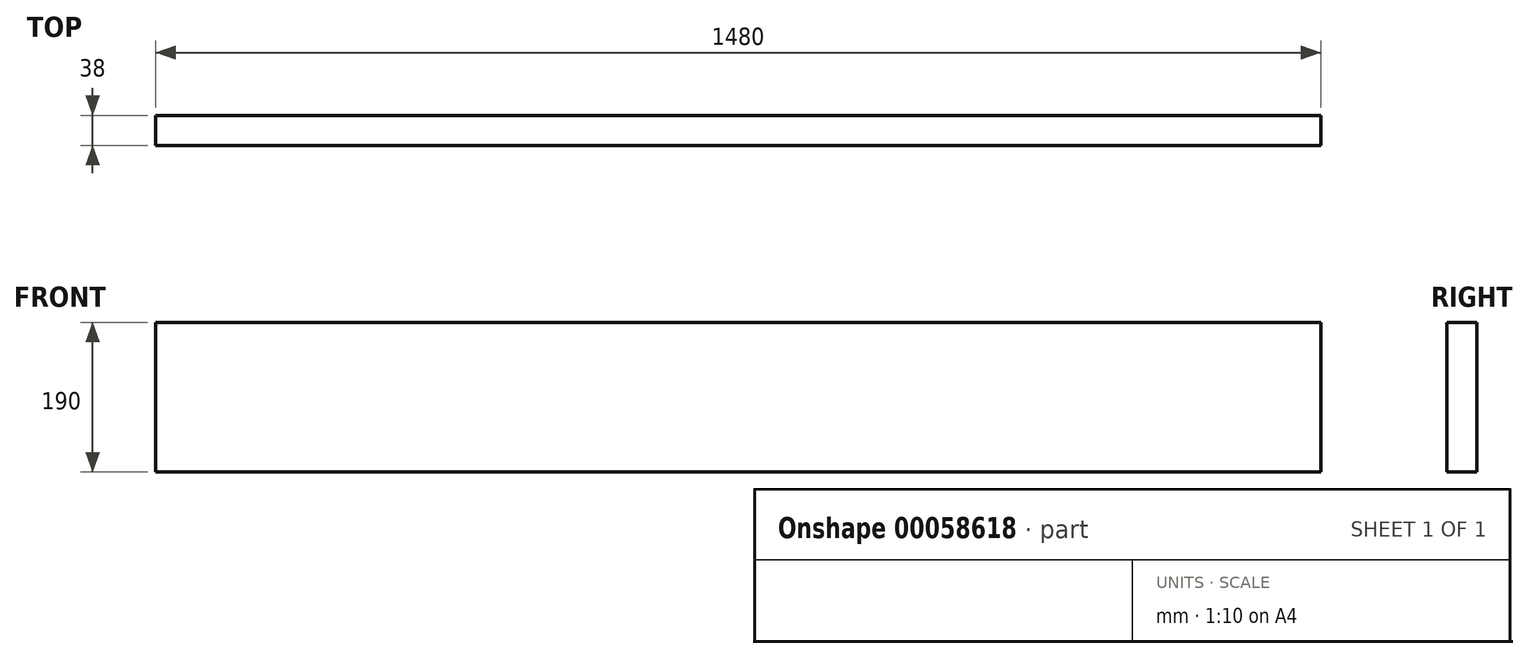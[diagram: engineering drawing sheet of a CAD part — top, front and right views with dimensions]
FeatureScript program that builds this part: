
annotation { "Feature Type Name" : "Feature", "Feature Type Description" : "" }
export const myFeature = defineFeature(function(context is Context, id is Id, definition is map)
    precondition{}
    {
        {
            var Q0;
            Q0=qCreatedBy(makeId("Front.planeOp"),FACE);
            var sketch = newSketch(context, id + "F0", { "sketchPlane" : qUnion([Q0])});
            skLineSegment(sketch, "E0.bottom", {"start": v(1480, 190) * mm, "end": v(0, 190) * mm});
            skLineSegment(sketch, "E0.top", {"start": v(1480, 0) * mm, "end": v(0, 0) * mm});
            skLineSegment(sketch, "E0.left", {"start": v(1480, 190) * mm, "end": v(1480, 0) * mm});
            skLineSegment(sketch, "E0.right", {"start": v(0, 190) * mm, "end": v(0, 0) * mm});
            skSolve(sketch);
        }
        {
            var Q0;
            Q0=makeQuery(id+"F0.imprint","IMPRINT",FACE,{"disambiguationData":[TD([[makeQuery(id+"F0.imprint","IMPRINT",EDGE,{"derivedFrom":sQuery(id+"F0.wireOp",EDGE,"E0.bottom")}),1.0]])]});
            extrude(context, id + "F1", {"entities" : qUnion([Q0]), "depth" : 38 * mm});
        }
    });
